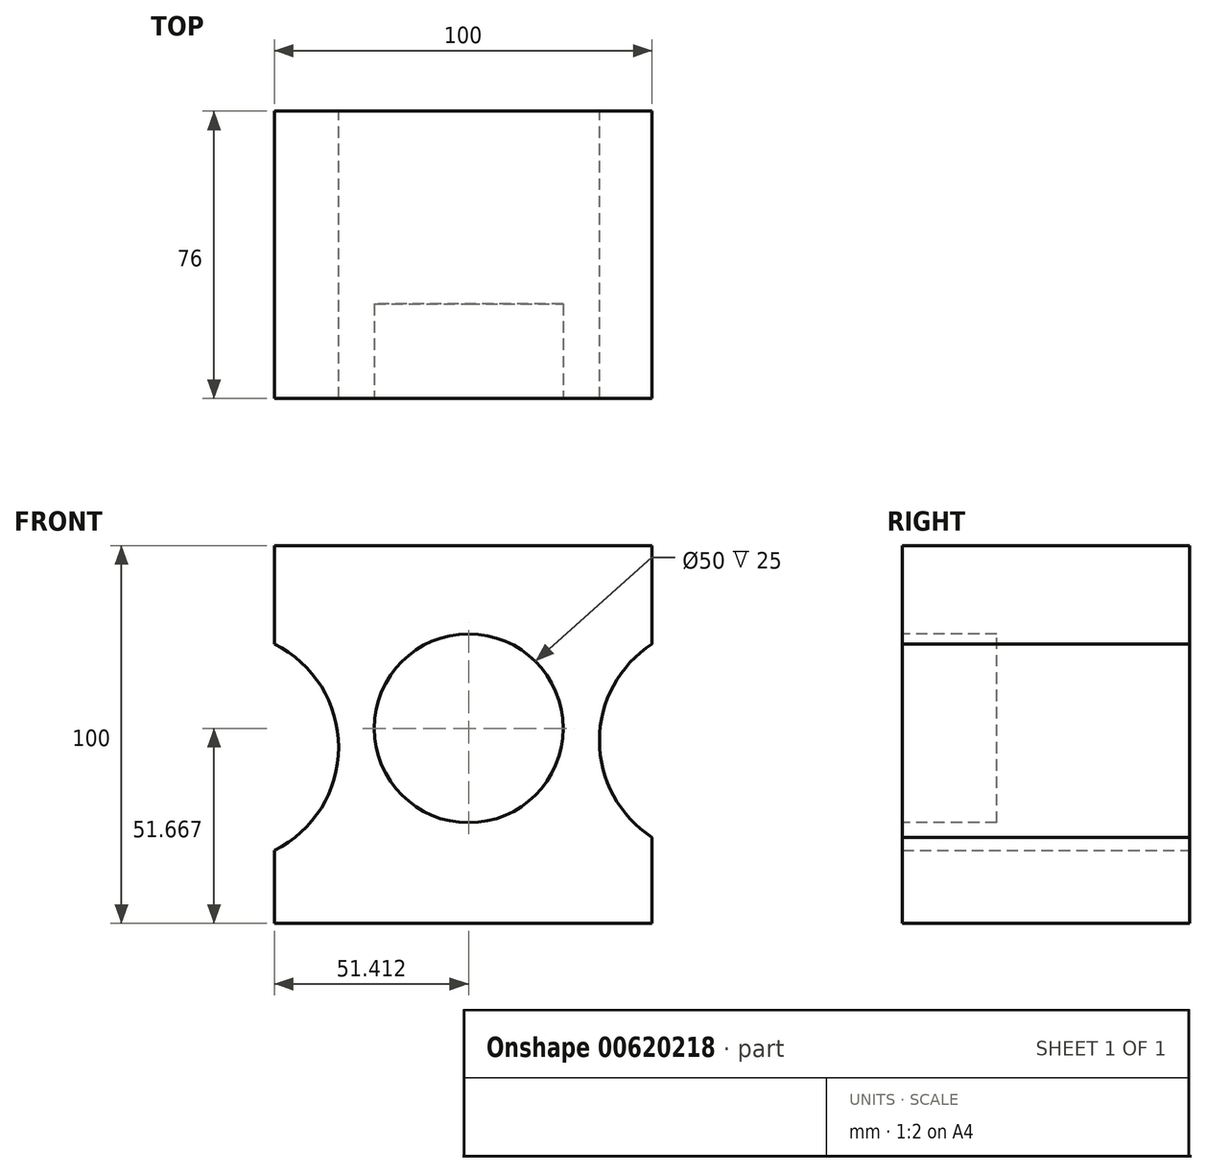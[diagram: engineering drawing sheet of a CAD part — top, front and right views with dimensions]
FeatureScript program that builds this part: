
annotation { "Feature Type Name" : "Feature", "Feature Type Description" : "" }
export const myFeature = defineFeature(function(context is Context, id is Id, definition is map)
    precondition{}
    {
        {
            var Q0;
            Q0=qCreatedBy(makeId("Front.planeOp"),FACE);
            var sketch = newSketch(context, id + "F0", { "sketchPlane" : qUnion([Q0])});
            skLineSegment(sketch, "E0.bottom", {"start": v(-46.02, 42.7) * mm, "end": v(53.98, 42.7) * mm});
            skLineSegment(sketch, "E0.top", {"start": v(-46.02, -57.3) * mm, "end": v(53.98, -57.3) * mm});
            skLineSegment(sketch, "E0.left", {"start": v(-46.02, 42.7) * mm, "end": v(-46.02, 16.68) * mm});
            skLineSegment(sketch, "E0.right", {"start": v(53.98, 42.7) * mm, "end": v(53.98, 16.68) * mm});
            skArc(sketch, "E1", {"start": v(53.98, 16.68) * mm, "mid": v(40.03, -8.9) * mm, "end": v(53.98, -34.48) * mm});
            skArc(sketch, "E2", {"start": v(-46.02, -38) * mm, "mid": v(-29.03, -10.66) * mm, "end": v(-46.02, 16.68) * mm});
            skLineSegment(sketch, "E3.trimOffspring", {"start": v(-46.02, -38) * mm, "end": v(-46.02, -57.3) * mm});
            skLineSegment(sketch, "E4.trimOffspring", {"start": v(53.98, -34.48) * mm, "end": v(53.98, -57.3) * mm});
            skSolve(sketch);
        }
        {
            var Q0;
            Q0=makeQuery(id+"F0.imprint","IMPRINT",FACE,{"disambiguationData":[TD([[makeQuery(id+"F0.imprint","IMPRINT",EDGE,{"derivedFrom":sQuery(id+"F0.wireOp",EDGE,"E0.bottom")}),-1.0]])]});
            extrude(context, id + "F1", {"entities" : qUnion([Q0]), "depth" : 60 * mm, "offsetDistance" : 25 * mm});
        }
        {
            var Q0;
            Q0=makeQuery(id+"F1.opExtrude","CAP_FACE",FACE,{"disambiguationData":[OSD([sQuery(id+"F0.wireOp",EDGE,"E0.bottom"),sQuery(id+"F0.wireOp",EDGE,"E0.top"),sQuery(id+"F0.wireOp",EDGE,"E0.left"),sQuery(id+"F0.wireOp",EDGE,"E0.right"),sQuery(id+"F0.wireOp",EDGE,"E1"),sQuery(id+"F0.wireOp",EDGE,"E2"),sQuery(id+"F0.wireOp",EDGE,"E3.trimOffspring"),sQuery(id+"F0.wireOp",EDGE,"E4.trimOffspring")])],"isStart":false});
            extrude(context, id + "F2", {"entities" : qUnion([Q0]), "operationType" : NewBodyOperationType.ADD, "depth" : 16 * mm, "offsetDistance" : 25 * mm});
        }
        {
            var Q0;
            Q0=makeQuery(id+"F2.opExtrude","CAP_FACE",FACE,{"disambiguationData":[OSD([sQuery(id+"F0.wireOp",EDGE,"E0.bottom"),sQuery(id+"F0.wireOp",EDGE,"E0.top"),sQuery(id+"F0.wireOp",EDGE,"E0.left"),sQuery(id+"F0.wireOp",EDGE,"E0.right"),sQuery(id+"F0.wireOp",EDGE,"E1"),sQuery(id+"F0.wireOp",EDGE,"E2"),sQuery(id+"F0.wireOp",EDGE,"E3.trimOffspring"),sQuery(id+"F0.wireOp",EDGE,"E4.trimOffspring")])],"isStart":false});
            var sketch = newSketch(context, id + "F3", { "sketchPlane" : qUnion([Q0])});
            skCircle(sketch, "E5", {"center": v(5.4, -5.64) * mm, "radius": 25 * mm});
            skSolve(sketch);
        }
        {
            var Q0;
            Q0=makeQuery(id+"F3.imprint","IMPRINT",FACE,{"disambiguationData":[TD([[makeQuery(id+"F3.imprint","IMPRINT",EDGE,{"derivedFrom":sQuery(id+"F3.wireOp",EDGE,"E5")}),1.0]])]});
            extrude(context, id + "F4", {"entities" : qUnion([Q0]), "operationType" : NewBodyOperationType.REMOVE, "oppositeDirection" : true, "depth" : 25 * mm, "offsetDistance" : 25 * mm});
        }
    });
